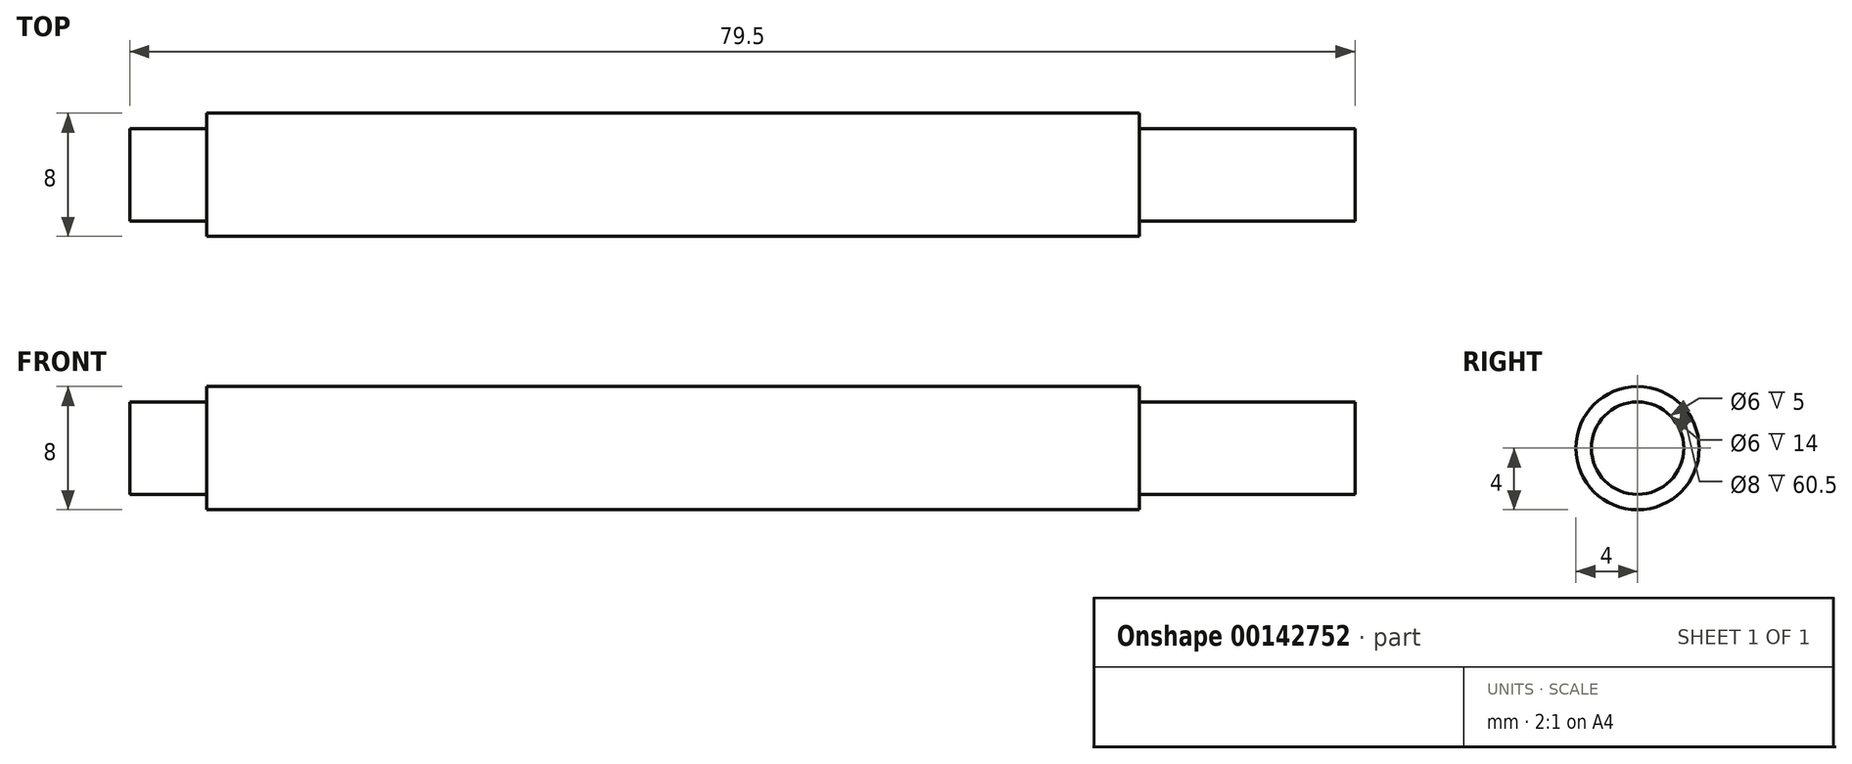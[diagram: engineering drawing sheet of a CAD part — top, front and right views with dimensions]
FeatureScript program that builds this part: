
annotation { "Feature Type Name" : "Feature", "Feature Type Description" : "" }
export const myFeature = defineFeature(function(context is Context, id is Id, definition is map)
    precondition{}
    {
        {
            var Q0;
            Q0=qCreatedBy(makeId("Front.planeOp"),FACE);
            var sketch = newSketch(context, id + "F0", { "sketchPlane" : qUnion([Q0])});
            skLineSegment(sketch, "E0", {"start": v(0, 0) * mm, "end": v(0, 3) * mm});
            skLineSegment(sketch, "E1", {"start": v(0, 3) * mm, "end": v(5, 3) * mm});
            skLineSegment(sketch, "E2", {"start": v(5, 3) * mm, "end": v(5, 4) * mm});
            skLineSegment(sketch, "E3", {"start": v(5, 4) * mm, "end": v(30.5, 4) * mm});
            skLineSegment(sketch, "E4", {"start": v(40.5, 4) * mm, "end": v(65.5, 4) * mm});
            skLineSegment(sketch, "E5", {"start": v(65.5, 4) * mm, "end": v(65.5, 3) * mm});
            skLineSegment(sketch, "E6", {"start": v(65.5, 3) * mm, "end": v(79.5, 3) * mm});
            skLineSegment(sketch, "E7", {"start": v(79.5, 3) * mm, "end": v(79.5, 0) * mm});
            skLineSegment(sketch, "E8", {"start": v(0, 0) * mm, "end": v(114.7, 0) * mm, "construction": true});
            skLineSegment(sketch, "E9", {"start": v(40.5, 4) * mm, "end": v(30.5, 4) * mm});
            skSolve(sketch);
        }
        {
            var Q0;
            Q0=sQuery(id+"F0.wireOp",EDGE,"E0");
            var Q1;
            Q1=sQuery(id+"F0.wireOp",EDGE,"E1");
            var Q2;
            Q2=sQuery(id+"F0.wireOp",EDGE,"E2");
            var Q3;
            Q3=sQuery(id+"F0.wireOp",EDGE,"E3");
            var Q4;
            Q4=sQuery(id+"F0.wireOp",EDGE,"E4");
            var Q5;
            Q5=sQuery(id+"F0.wireOp",EDGE,"E9");
            var Q6;
            Q6=sQuery(id+"F0.wireOp",EDGE,"E5");
            var Q7;
            Q7=sQuery(id+"F0.wireOp",EDGE,"E6");
            var Q8;
            Q8=sQuery(id+"F0.wireOp",EDGE,"E7");
            var Q9;
            Q9=sQuery(id+"F0.wireOp",EDGE,"E8");
            revolve(context, id + "F1", {"bodyType" : ToolBodyType.SURFACE, "surfaceEntities" : qUnion([Q0, Q1, Q2, Q3, Q4, Q5, Q6, Q7, Q8]), "axis" : qUnion([Q9]), "revolveType" : RevolveType.FULL});
        }
    });
